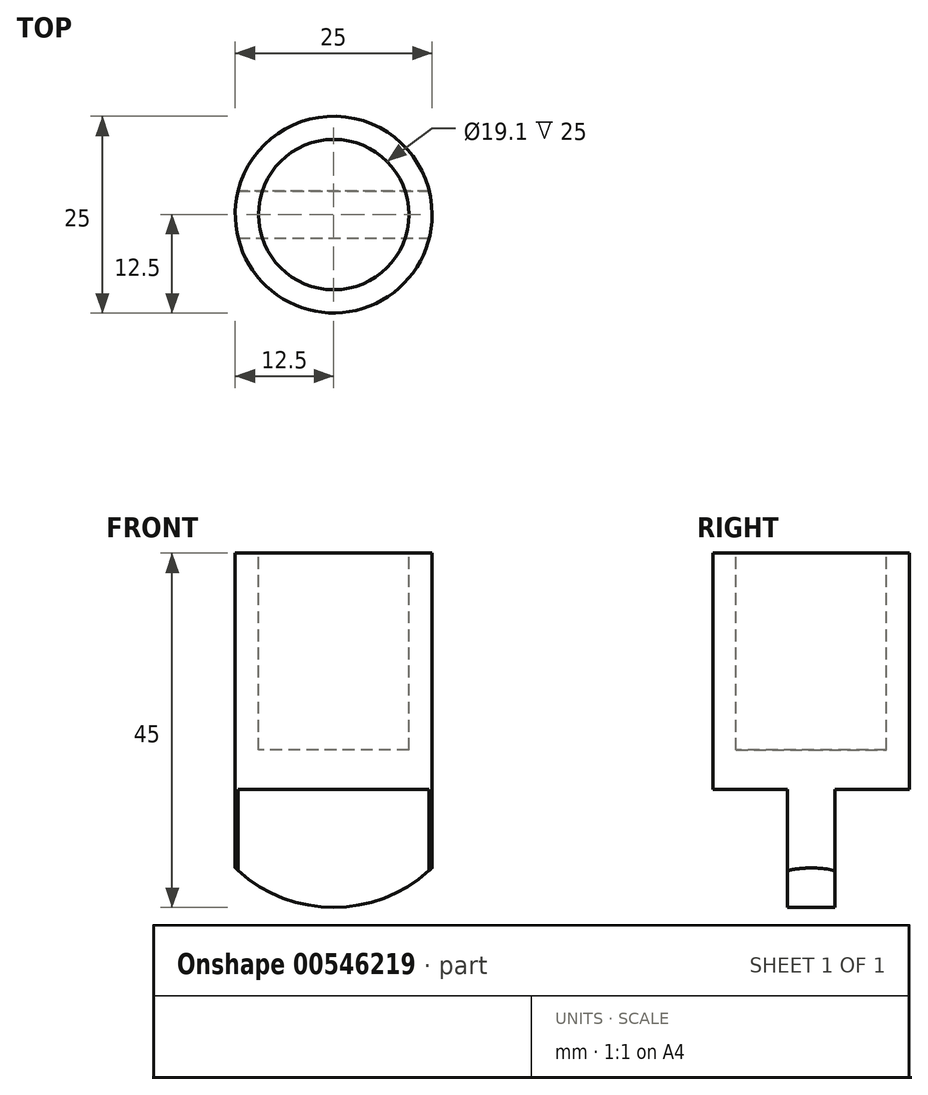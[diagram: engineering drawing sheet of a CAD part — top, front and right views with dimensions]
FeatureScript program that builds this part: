
annotation { "Feature Type Name" : "Feature", "Feature Type Description" : "" }
export const myFeature = defineFeature(function(context is Context, id is Id, definition is map)
    precondition{}
    {
        {
            var Q0;
            Q0=qCreatedBy(makeId("Top.planeOp"),FACE);
            var sketch = newSketch(context, id + "F0", { "sketchPlane" : qUnion([Q0])});
            skCircle(sketch, "E0", {"center": v(0, 0) * mm, "radius": 12.5 * mm});
            skSolve(sketch);
        }
        {
            var Q0;
            Q0 = qSketchRegion(id + "F0", true);
            extrude(context, id + "F1", {"entities" : qUnion([Q0]), "depth" : 30 * mm, "offsetDistance" : 25 * mm});
        }
        {
            var Q0;
            Q0=makeQuery(id+"F1.opExtrude","CAP_FACE",FACE,{"disambiguationData":[OSD([sQuery(id+"F0.wireOp",EDGE,"E0")])],"isStart":false});
            var sketch = newSketch(context, id + "F2", { "sketchPlane" : qUnion([Q0])});
            skCircle(sketch, "E1", {"center": v(0, 0) * mm, "radius": 9.55 * mm});
            skSolve(sketch);
        }
        {
            var Q0;
            Q0 = qSketchRegion(id + "F2", true);
            extrude(context, id + "F3", {"entities" : qUnion([Q0]), "operationType" : NewBodyOperationType.REMOVE, "oppositeDirection" : true, "depth" : 25 * mm, "offsetDistance" : 25 * mm});
        }
        {
            var Q0;
            Q0=makeQuery(id+"F1.opExtrude","CAP_FACE",FACE,{"disambiguationData":[OSD([sQuery(id+"F0.wireOp",EDGE,"E0")])],"isStart":true});
            var sketch = newSketch(context, id + "F4", { "sketchPlane" : qUnion([Q0])});
            skLineSegment(sketch, "E2", {"start": v(-12.13, 3) * mm, "end": v(12.13, 3) * mm});
            skLineSegment(sketch, "E3", {"start": v(-12.13, -3) * mm, "end": v(12.13, -3) * mm});
            skArc(sketch, "E4", {"start": v(-12.13, 3) * mm, "mid": v(-12.5, 0) * mm, "end": v(-12.13, -3) * mm});
            skArc(sketch, "E5", {"start": v(12.13, -3) * mm, "mid": v(12.5, 0) * mm, "end": v(12.13, 3) * mm});
            skSolve(sketch);
        }
        {
            var Q0;
            Q0=makeQuery(id+"F4.imprint","IMPRINT",FACE,{"disambiguationData":[TD([[makeQuery(id+"F4.imprint","IMPRINT",EDGE,{"derivedFrom":sQuery(id+"F4.wireOp",EDGE,"E2")}),-1.0]])]});
            extrude(context, id + "F5", {"entities" : qUnion([Q0]), "operationType" : NewBodyOperationType.ADD, "depth" : 15 * mm, "offsetDistance" : 25 * mm});
        }
        {
            var Q0;
            Q0=makeQuery(id+"F5.opExtrude","SWEPT_FACE",FACE,{"disambiguationData":[OSD([sQuery(id+"F4.wireOp",EDGE,"E3")])]});
            var sketch = newSketch(context, id + "F6", { "sketchPlane" : qUnion([Q0])});
            skArc(sketch, "E6", {"start": v(-12.5, -10) * mm, "mid": v(0, -15) * mm, "end": v(12.5, -10) * mm});
            skLineSegment(sketch, "E7", {"start": v(12.5, -15) * mm, "end": v(-12.5, -15) * mm});
            skLineSegment(sketch, "E8", {"start": v(12.5, -10) * mm, "end": v(-12.5, -10) * mm, "construction": true});
            skPoint(sketch, "E9", {"position": v(0, -10) * mm});
            skLineSegment(sketch, "E10", {"start": v(-12.5, -15) * mm, "end": v(-12.5, -10) * mm});
            skLineSegment(sketch, "E11", {"start": v(12.5, -10) * mm, "end": v(12.5, -15) * mm});
            skSolve(sketch);
        }
        {
            var Q0;
            Q0 = qSketchRegion(id + "F6", true);
            extrude(context, id + "F7", {"entities" : qUnion([Q0]), "operationType" : NewBodyOperationType.REMOVE, "oppositeDirection" : true, "depth" : 25 * mm, "offsetDistance" : 25 * mm});
        }
    });
